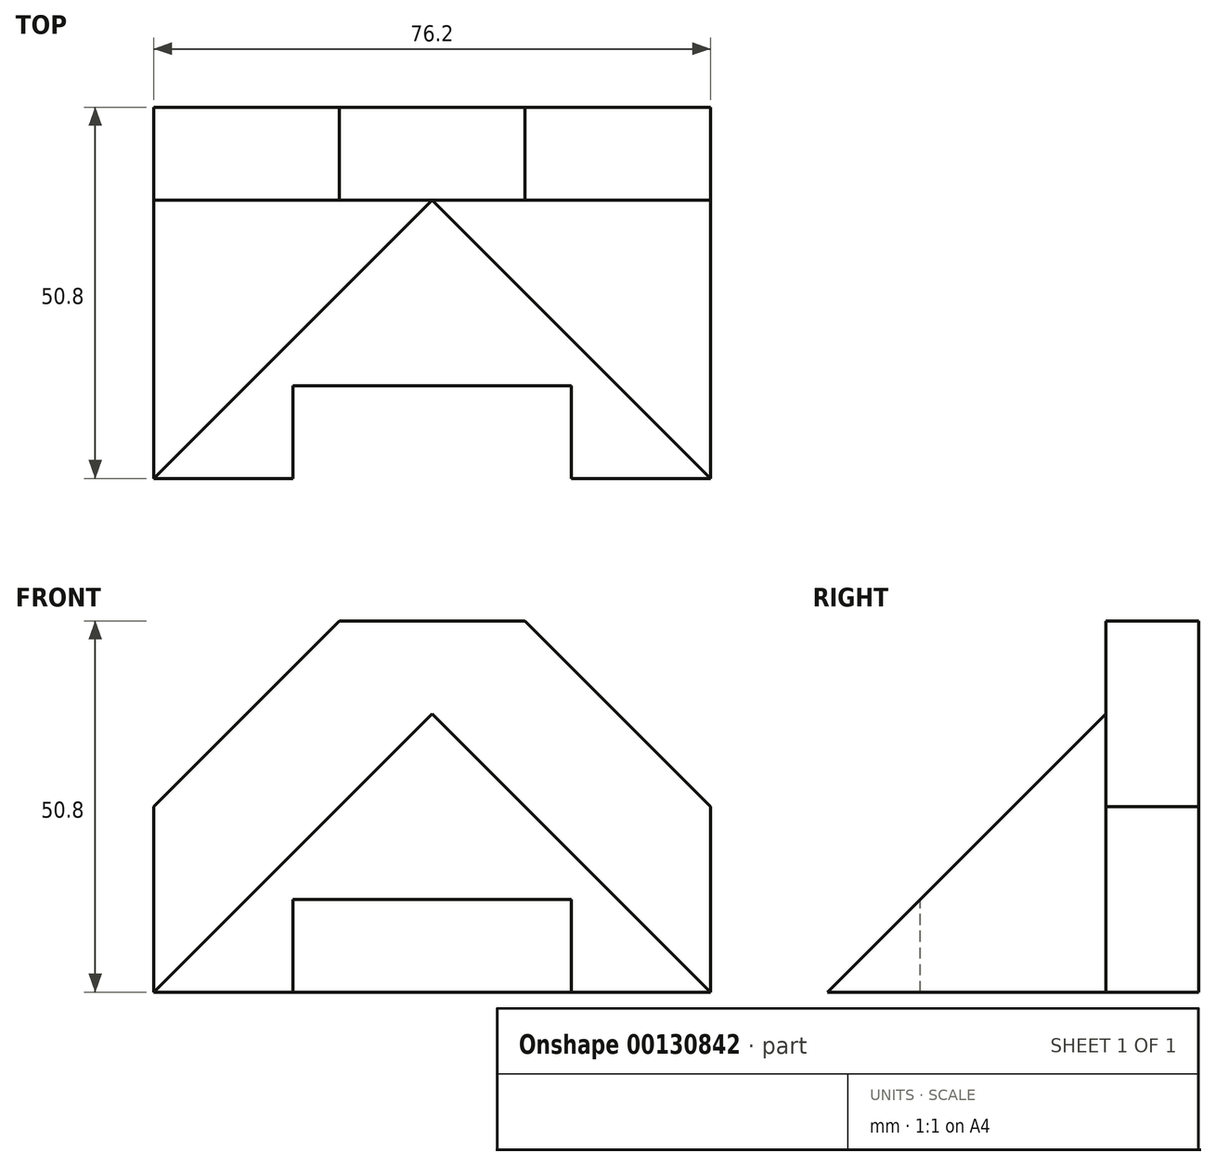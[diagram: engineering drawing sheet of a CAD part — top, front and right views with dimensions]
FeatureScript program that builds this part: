
annotation { "Feature Type Name" : "Feature", "Feature Type Description" : "" }
export const myFeature = defineFeature(function(context is Context, id is Id, definition is map)
    precondition{}
    {
        {
            var Q0;
            Q0=qCreatedBy(makeId("Front.planeOp"),FACE);
            var sketch = newSketch(context, id + "F0", { "sketchPlane" : qUnion([Q0])});
            skLineSegment(sketch, "E0", {"start": v(0, 65.66) * mm, "end": v(0, -47.84) * mm, "construction": true});
            skLineSegment(sketch, "E1", {"start": v(-38.1, 0) * mm, "end": v(-38.1, 25.4) * mm});
            skLineSegment(sketch, "E2", {"start": v(-38.1, 25.4) * mm, "end": v(-12.7, 50.8) * mm});
            skLineSegment(sketch, "E3", {"start": v(-12.7, 50.8) * mm, "end": v(12.7, 50.8) * mm});
            skLineSegment(sketch, "E4", {"start": v(12.7, 50.8) * mm, "end": v(38.1, 25.4) * mm});
            skLineSegment(sketch, "E5", {"start": v(38.1, 25.4) * mm, "end": v(38.1, 0) * mm});
            skLineSegment(sketch, "E6", {"start": v(38.1, 0) * mm, "end": v(0, 38.1) * mm});
            skLineSegment(sketch, "E7", {"start": v(0, 38.1) * mm, "end": v(-38.1, 0) * mm});
            skLineSegment(sketch, "E8.bottom", {"start": v(-19.05, 0) * mm, "end": v(19.05, 0) * mm});
            skLineSegment(sketch, "E8.top", {"start": v(-19.05, 12.7) * mm, "end": v(19.05, 12.7) * mm});
            skLineSegment(sketch, "E8.left", {"start": v(-19.05, 0) * mm, "end": v(-19.05, 12.7) * mm});
            skLineSegment(sketch, "E8.right", {"start": v(19.05, 0) * mm, "end": v(19.05, 12.7) * mm});
            skLineSegment(sketch, "E9", {"start": v(-38.1, 0) * mm, "end": v(38.1, 0) * mm});
            skSolve(sketch);
        }
        {
            var Q0;
            {var subQ2=sQuery(id+"F0.wireOp",EDGE,"E6");Q0=makeQuery(id+"F0.imprint","IMPRINT",FACE,{"disambiguationData":[TD([[makeQuery(id+"F0.imprint","IMPRINT",EDGE,{"derivedFrom":subQ2}),1.0]])]});}
            extrude(context, id + "F1", {"entities" : qUnion([Q0]), "depth" : 38.1 * mm});
        }
        {
            var Q0;
            Q0=makeQuery(id+"F0.imprint","IMPRINT",FACE,{"disambiguationData":[TD([[makeQuery(id+"F0.imprint","IMPRINT",EDGE,{"derivedFrom":sQuery(id+"F0.wireOp",EDGE,"E1")}),-1.0]])]});
            var Q1;
            {var subQ2=sQuery(id+"F0.wireOp",EDGE,"E6");Q1=makeQuery(id+"F0.imprint","IMPRINT",FACE,{"disambiguationData":[TD([[makeQuery(id+"F0.imprint","IMPRINT",EDGE,{"derivedFrom":subQ2}),1.0]])]});}
            var Q2;
            Q2=makeQuery(id+"F0.imprint","IMPRINT",FACE,{"disambiguationData":[TD([[makeQuery(id+"F0.imprint","IMPRINT",EDGE,{"derivedFrom":sQuery(id+"F0.wireOp",EDGE,"E8.top")}),-1.0]])]});
            extrude(context, id + "F2", {"entities" : qUnion([Q0, Q1, Q2]), "operationType" : NewBodyOperationType.ADD, "oppositeDirection" : true, "depth" : 12.7 * mm});
        }
        {
            var Q0;
            Q0=makeQuery(id+"F2.opExtrude","SWEPT_FACE",FACE,{"disambiguationData":[OSD([sQuery(id+"F0.wireOp",EDGE,"E5")])]});
            var sketch = newSketch(context, id + "F3", { "sketchPlane" : qUnion([Q0])});
            skLineSegment(sketch, "E10.0", {"start": v(-38.1, 0) * mm, "end": v(-38.1, 38.1) * mm});
            skLineSegment(sketch, "E11.0", {"start": v(-38.1, 38.1) * mm, "end": v(0, 38.1) * mm});
            skLineSegment(sketch, "E12", {"start": v(-38.1, 0) * mm, "end": v(0, 38.1) * mm});
            skSolve(sketch);
        }
        {
            var Q0;
            Q0=makeQuery(id+"F3.imprint","IMPRINT",FACE,{"disambiguationData":[TD([[makeQuery(id+"F3.imprint","IMPRINT",EDGE,{"derivedFrom":sQuery(id+"F3.wireOp",EDGE,"E10.0")}),-1.0]])]});
            extrude(context, id + "F4", {"entities" : qUnion([Q0]), "operationType" : NewBodyOperationType.REMOVE, "endBound" : BoundingType.THROUGH_ALL, "oppositeDirection" : true, "depth" : 25.4 * mm});
        }
        {
            var Q0;
            Q0=makeQuery(id+"F0.imprint","IMPRINT",FACE,{"disambiguationData":[TD([[makeQuery(id+"F0.imprint","IMPRINT",EDGE,{"derivedFrom":sQuery(id+"F0.wireOp",EDGE,"E8.top")}),-1.0]])]});
            extrude(context, id + "F5", {"entities" : qUnion([Q0]), "operationType" : NewBodyOperationType.ADD, "depth" : 25.4 * mm});
        }
    });
